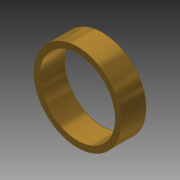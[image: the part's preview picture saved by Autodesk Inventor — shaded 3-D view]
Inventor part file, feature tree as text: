
AUTODESK INVENTOR PART (.ipt)
format: ipt  version: 2014 SP1 (Build 180222100, 222)  size: 87,040 bytes
history: native  units: in
note: dims shown in document units (in); Inventor stores cm internally (conversion verified against a paired STEP export)
features: extrude x1, sketch x1
ambient origin geometry x8: Origin, YZ Plane, XZ Plane, XY Plane, X Axis, Y Axis, Z Axis, Center Point
bodies: Solid1 (feature_tree)
feature tree (2):
  extrude  "Extrusion1"  Depth=0.125in
  sketch  "Sketch1"  dims[d0=0.379in d2=0.437in d3=0.125in d4=0.0in]
